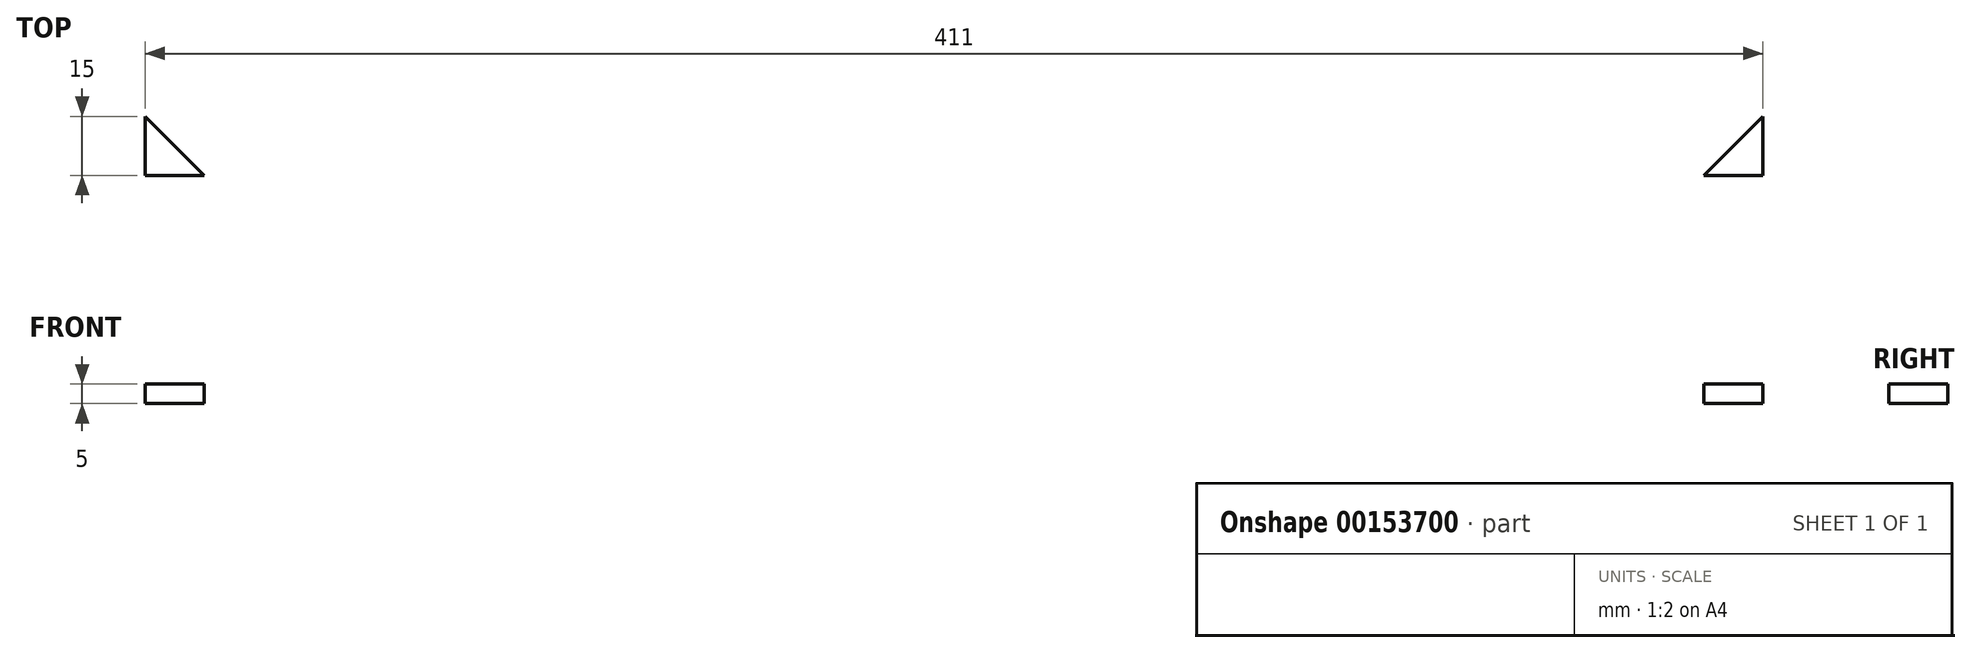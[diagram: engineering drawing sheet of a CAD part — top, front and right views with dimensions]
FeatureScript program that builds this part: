
annotation { "Feature Type Name" : "Feature", "Feature Type Description" : "" }
export const myFeature = defineFeature(function(context is Context, id is Id, definition is map)
    precondition{}
    {
        {
            var Q0;
            Q0=qCreatedBy(makeId("Top.planeOp"),FACE);
            var sketch = newSketch(context, id + "F0", { "sketchPlane" : qUnion([Q0])});
            skLineSegment(sketch, "E0.bottom", {"start": v(-21.93, 0) * mm, "end": v(389.07, 0) * mm});
            skLineSegment(sketch, "E0.top", {"start": v(-21.93, 372) * mm, "end": v(389.07, 372) * mm});
            skLineSegment(sketch, "E0.left", {"start": v(-21.93, 0) * mm, "end": v(-21.93, 372) * mm});
            skLineSegment(sketch, "E0.right", {"start": v(389.07, 0) * mm, "end": v(389.07, 372) * mm});
            skLineSegment(sketch, "E1", {"start": v(-21.93, 15) * mm, "end": v(-6.93, 0) * mm});
            skLineSegment(sketch, "E2", {"start": v(-21.93, 357) * mm, "end": v(-6.93, 372) * mm});
            skLineSegment(sketch, "E3", {"start": v(374.07, 372) * mm, "end": v(389.07, 357) * mm});
            skLineSegment(sketch, "E4", {"start": v(374.07, 0) * mm, "end": v(389.07, 15) * mm});
            skLineSegment(sketch, "E5", {"start": v(-21.93, 0) * mm, "end": v(-6.93, 0) * mm});
            skLineSegment(sketch, "E6", {"start": v(-21.93, 0) * mm, "end": v(-21.93, 15) * mm});
            skLineSegment(sketch, "E7", {"start": v(-21.93, 357) * mm, "end": v(-21.93, 372) * mm});
            skLineSegment(sketch, "E8", {"start": v(-6.93, 372) * mm, "end": v(-21.93, 372) * mm});
            skLineSegment(sketch, "E9", {"start": v(374.07, 372) * mm, "end": v(389.07, 372) * mm});
            skLineSegment(sketch, "E10", {"start": v(389.07, 357) * mm, "end": v(389.07, 372) * mm});
            skLineSegment(sketch, "E11", {"start": v(389.07, 0) * mm, "end": v(389.07, 15) * mm});
            skLineSegment(sketch, "E12", {"start": v(374.07, 0) * mm, "end": v(389.07, 0) * mm});
            skLineSegment(sketch, "E13", {"start": v(389.07, 15) * mm, "end": v(389.07, 0) * mm});
            skLineSegment(sketch, "E14", {"start": v(389.07, 0) * mm, "end": v(374.07, 0) * mm});
            skSolve(sketch);
        }
        {
            var Q0;
            Q0=makeQuery(id+"F0.imprint","IMPRINT",FACE,{"disambiguationData":[TD([[makeQuery(id+"F0.imprint","IMPRINT",EDGE,{"derivedFrom":sQuery(id+"F0.wireOp",EDGE,"E0.bottom")}),1.0]])]});
            extrude(context, id + "F1", {"entities" : qUnion([Q0]), "depth" : 5 * mm});
        }
    });
